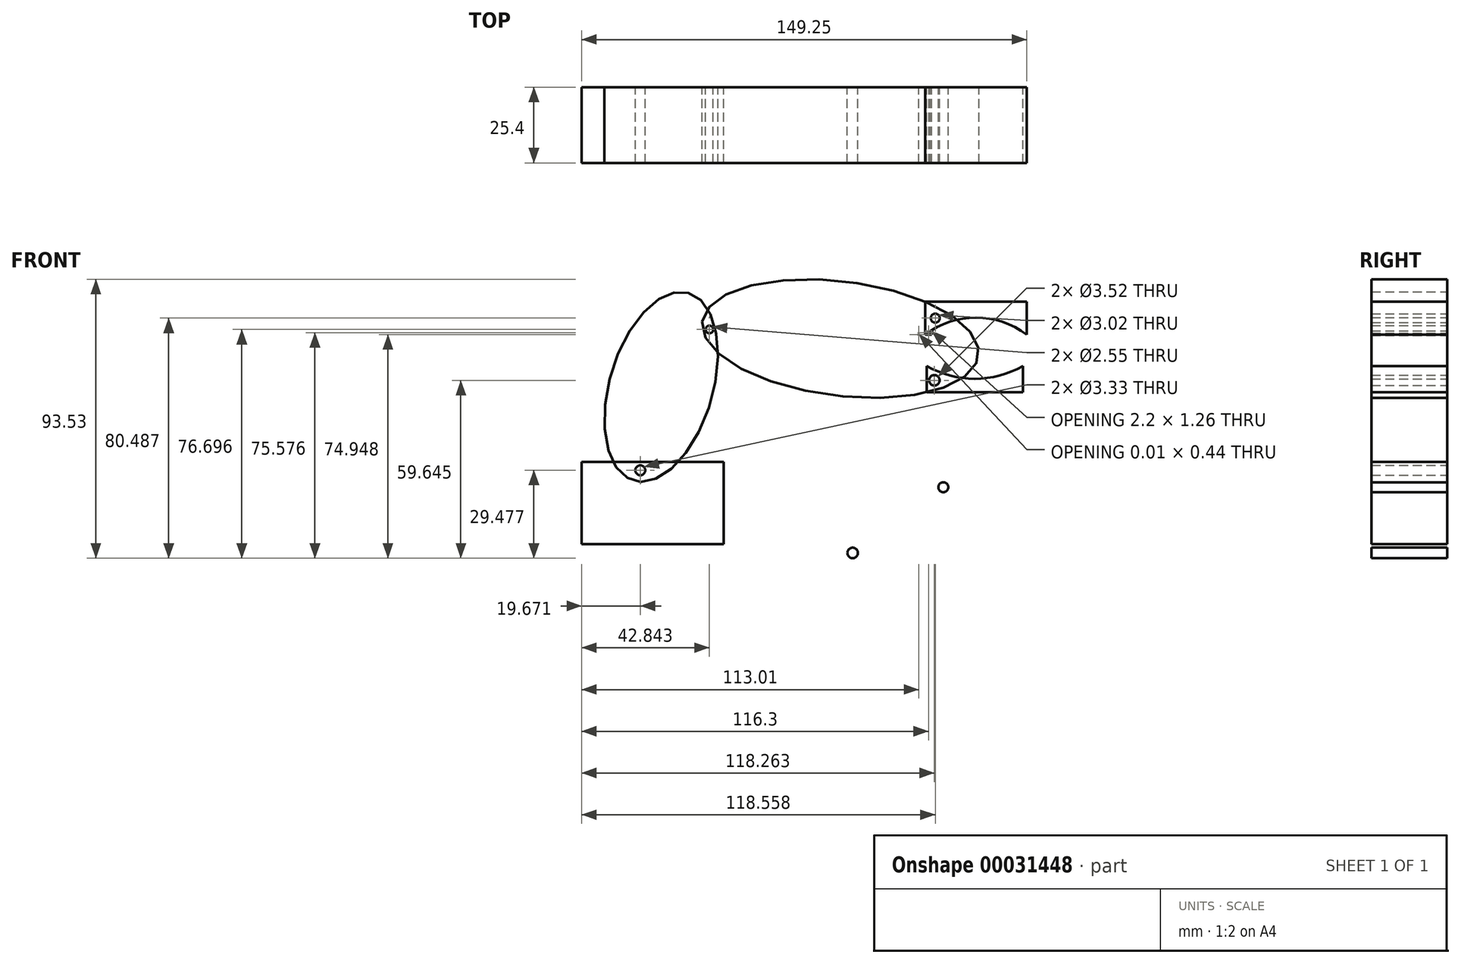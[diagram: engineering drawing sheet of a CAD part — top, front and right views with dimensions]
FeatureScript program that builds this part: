
annotation { "Feature Type Name" : "Feature", "Feature Type Description" : "" }
export const myFeature = defineFeature(function(context is Context, id is Id, definition is map)
    precondition{}
    {
        {
            var Q0;
            Q0=qCreatedBy(makeId("Front.planeOp"),FACE);
            var sketch = newSketch(context, id + "F0", { "sketchPlane" : qUnion([Q0])});
            skLineSegment(sketch, "E0.bottom", {"start": v(-76.3, -14) * mm, "end": v(-28.64, -14) * mm});
            skLineSegment(sketch, "E0.top", {"start": v(-76.3, -41.54) * mm, "end": v(-28.64, -41.54) * mm});
            skLineSegment(sketch, "E0.left", {"start": v(-76.3, -14) * mm, "end": v(-76.3, -41.54) * mm});
            skLineSegment(sketch, "E0.right", {"start": v(-28.64, -14) * mm, "end": v(-28.64, -41.54) * mm});
            skEllipse(sketch, "E1", {"center": v(-49.62, 11.15) * mm, "majorRadius": 32.8 * mm, "minorRadius": 17.35 * mm, "majorAxis": v(0.28, 0.96)});
            skEllipse(sketch, "E2", {"center": v(10.5, 27.33) * mm, "majorRadius": 46.7 * mm, "minorRadius": 19.2 * mm, "majorAxis": v(-1, 0.12)});
            skLineSegment(sketch, "E3.top", {"start": v(39.35, 9.4) * mm, "end": v(71.7, 9.4) * mm});
            skLineSegment(sketch, "E3.left", {"start": v(39.35, 18.14) * mm, "end": v(39.35, 9.4) * mm});
            skLineSegment(sketch, "E3.right", {"start": v(71.7, 18.14) * mm, "end": v(71.7, 9.4) * mm});
            skLineSegment(sketch, "E4.left", {"start": v(36.73, 28.86) * mm, "end": v(36.73, 28.42) * mm});
            skArc(sketch, "E5", {"start": v(39.35, 18.14) * mm, "mid": v(55.53, 13.85) * mm, "end": v(71.7, 18.14) * mm});
            skCircle(sketch, "E6", {"center": v(-56.62, -16.83) * mm, "radius": 1.66 * mm});
            skCircle(sketch, "E7", {"center": v(-33.45, 30.39) * mm, "radius": 1.27 * mm});
            skArc(sketch, "E8", {"start": v(41.1, 28.64) * mm, "mid": v(41, 29.3) * mm, "end": v(40.71, 29.9) * mm});
            skCircle(sketch, "E9", {"center": v(41.97, 13.34) * mm, "radius": 1.76 * mm});
            skLineSegment(sketch, "E10.bottom", {"start": v(38.91, 39.72) * mm, "end": v(72.96, 39.72) * mm});
            skLineSegment(sketch, "E10.top", {"start": v(38.91, 28.64) * mm, "end": v(41.1, 28.64) * mm});
            skLineSegment(sketch, "E10.left", {"start": v(38.91, 39.72) * mm, "end": v(38.91, 28.64) * mm});
            skLineSegment(sketch, "E10.right", {"start": v(72.96, 39.72) * mm, "end": v(72.96, 28.64) * mm});
            skArc(sketch, "E11", {"start": v(72.96, 28.64) * mm, "mid": v(55.94, 34.35) * mm, "end": v(38.91, 28.64) * mm});
            skArc(sketch, "E12.trimOffspring", {"start": v(36.73, 28.86) * mm, "mid": v(36.71, 28.64) * mm, "end": v(36.73, 28.42) * mm});
            skCircle(sketch, "E13", {"center": v(42.27, 34.18) * mm, "radius": 1.5 * mm});
            skPoint(sketch, "E13.centerSnap0", {"position": v(38.91, 34.18) * mm});
            skCircle(sketch, "E14", {"center": v(44.95, -22.5) * mm, "radius": 1.66 * mm});
            skCircle(sketch, "E15", {"center": v(14.55, -44.55) * mm, "radius": 1.77 * mm});
            skSolve(sketch);
        }
        {
            var Q0;
            Q0=makeQuery(id+"F0.imprint","IMPRINT",FACE,{"disambiguationData":[TD([[makeQuery(id+"F0.imprint","IMPRINT",EDGE,{"derivedFrom":sQuery(id+"F0.wireOp",EDGE,"E0.top")}),1.0]])]});
            var Q1;
            Q1=makeQuery(id+"F0.imprint","IMPRINT",FACE,{"disambiguationData":[TD([[makeQuery(id+"F0.imprint","IMPRINT",EDGE,{"derivedFrom":sQuery(id+"F0.wireOp",EDGE,"E6")}),-1.0]])]});
            extrude(context, id + "F1", {"entities" : qUnion([Q0, Q1]), "depth" : 25.4 * mm});
        }
        {
            var Q0;
            {var subQ1=sQuery(id+"F0.wireOp",EDGE,"E1");var subQ4=sQuery(id+"F0.wireOp",EDGE,"E0.bottom");var subQ5=makeQuery(id+"F0.imprint","INTERSECT",VERTEX,{"disambiguationData":[OD(0.0)],"derivedFrom":[subQ4,subQ1]});Q0=makeQuery(id+"F0.imprint","IMPRINT",FACE,{"disambiguationData":[TD([[makeQuery(id+"F0.imprint","IMPRINT",EDGE,{"disambiguationData":[TD([[subQ5,-1.0]])],"derivedFrom":subQ4}),1.0]])]});}
            var Q1;
            Q1=makeQuery(id+"F0.imprint","IMPRINT",FACE,{"disambiguationData":[TD([[makeQuery(id+"F0.imprint","IMPRINT",EDGE,{"derivedFrom":sQuery(id+"F0.wireOp",EDGE,"E6")}),-1.0]])]});
            var Q2;
            Q2=makeQuery(id+"F0.imprint","IMPRINT",FACE,{"disambiguationData":[TD([[makeQuery(id+"F0.imprint","IMPRINT",EDGE,{"derivedFrom":sQuery(id+"F0.wireOp",EDGE,"E7")}),-1.0]])]});
            extrude(context, id + "F2", {"entities" : qUnion([Q0, Q1, Q2]), "depth" : 25.4 * mm});
        }
        {
            var Q0;
            {var subQ7=sQuery(id+"F0.wireOp",EDGE,"E3.left");Q0=makeQuery(id+"F0.imprint","IMPRINT",FACE,{"disambiguationData":[TD([[makeQuery(id+"F0.imprint","IMPRINT",EDGE,{"derivedFrom":subQ7}),-1.0]])]});}
            var Q1;
            Q1=makeQuery(id+"F0.imprint","IMPRINT",FACE,{"disambiguationData":[TD([[makeQuery(id+"F0.imprint","IMPRINT",EDGE,{"derivedFrom":sQuery(id+"F0.wireOp",EDGE,"E7")}),-1.0]])]});
            var Q2;
            {var subQ1=sQuery(id+"F0.wireOp",EDGE,"E10.left");Q2=makeQuery(id+"F0.imprint","IMPRINT",FACE,{"disambiguationData":[TD([[makeQuery(id+"F0.imprint","IMPRINT",EDGE,{"derivedFrom":subQ1}),1.0]])]});}
            var Q3;
            {var subQ3=sQuery(id+"F0.wireOp",EDGE,"E3.left");Q3=makeQuery(id+"F0.imprint","IMPRINT",FACE,{"disambiguationData":[TD([[makeQuery(id+"F0.imprint","IMPRINT",EDGE,{"derivedFrom":subQ3}),1.0]])]});}
            extrude(context, id + "F3", {"entities" : qUnion([Q0, Q1, Q2, Q3]), "depth" : 25.4 * mm});
        }
        {
            var Q0;
            {var subQ3=sQuery(id+"F0.wireOp",EDGE,"E3.right");Q0=makeQuery(id+"F0.imprint","IMPRINT",FACE,{"disambiguationData":[TD([[makeQuery(id+"F0.imprint","IMPRINT",EDGE,{"derivedFrom":subQ3}),-1.0]])]});}
            var Q1;
            {var subQ3=sQuery(id+"F0.wireOp",EDGE,"E3.left");Q1=makeQuery(id+"F0.imprint","IMPRINT",FACE,{"disambiguationData":[TD([[makeQuery(id+"F0.imprint","IMPRINT",EDGE,{"derivedFrom":subQ3}),1.0]])]});}
            extrude(context, id + "F4", {"entities" : qUnion([Q0, Q1]), "depth" : 25.4 * mm});
        }
        {
            var Q0;
            {var subQ4=sQuery(id+"F0.wireOp",EDGE,"E10.bottom");Q0=makeQuery(id+"F0.imprint","IMPRINT",FACE,{"disambiguationData":[TD([[makeQuery(id+"F0.imprint","IMPRINT",EDGE,{"derivedFrom":subQ4}),-1.0]])]});}
            var Q1;
            {var subQ1=sQuery(id+"F0.wireOp",EDGE,"E10.left");Q1=makeQuery(id+"F0.imprint","IMPRINT",FACE,{"disambiguationData":[TD([[makeQuery(id+"F0.imprint","IMPRINT",EDGE,{"derivedFrom":subQ1}),1.0]])]});}
            extrude(context, id + "F5", {"entities" : qUnion([Q0, Q1]), "depth" : 25.4 * mm});
        }
        {
            var Q0;
            Q0=makeQuery(id+"F0.imprint","IMPRINT",FACE,{"disambiguationData":[TD([[makeQuery(id+"F0.imprint","IMPRINT",EDGE,{"derivedFrom":sQuery(id+"F0.wireOp",EDGE,"E14")}),1.0]])]});
            extrude(context, id + "F6", {"entities" : qUnion([Q0]), "depth" : 25.4 * mm});
        }
        {
            var Q0;
            Q0=makeQuery(id+"F0.imprint","IMPRINT",FACE,{"disambiguationData":[TD([[makeQuery(id+"F0.imprint","IMPRINT",EDGE,{"derivedFrom":sQuery(id+"F0.wireOp",EDGE,"E15")}),1.0]])]});
            extrude(context, id + "F7", {"entities" : qUnion([Q0]), "depth" : 25.4 * mm});
        }
    });
